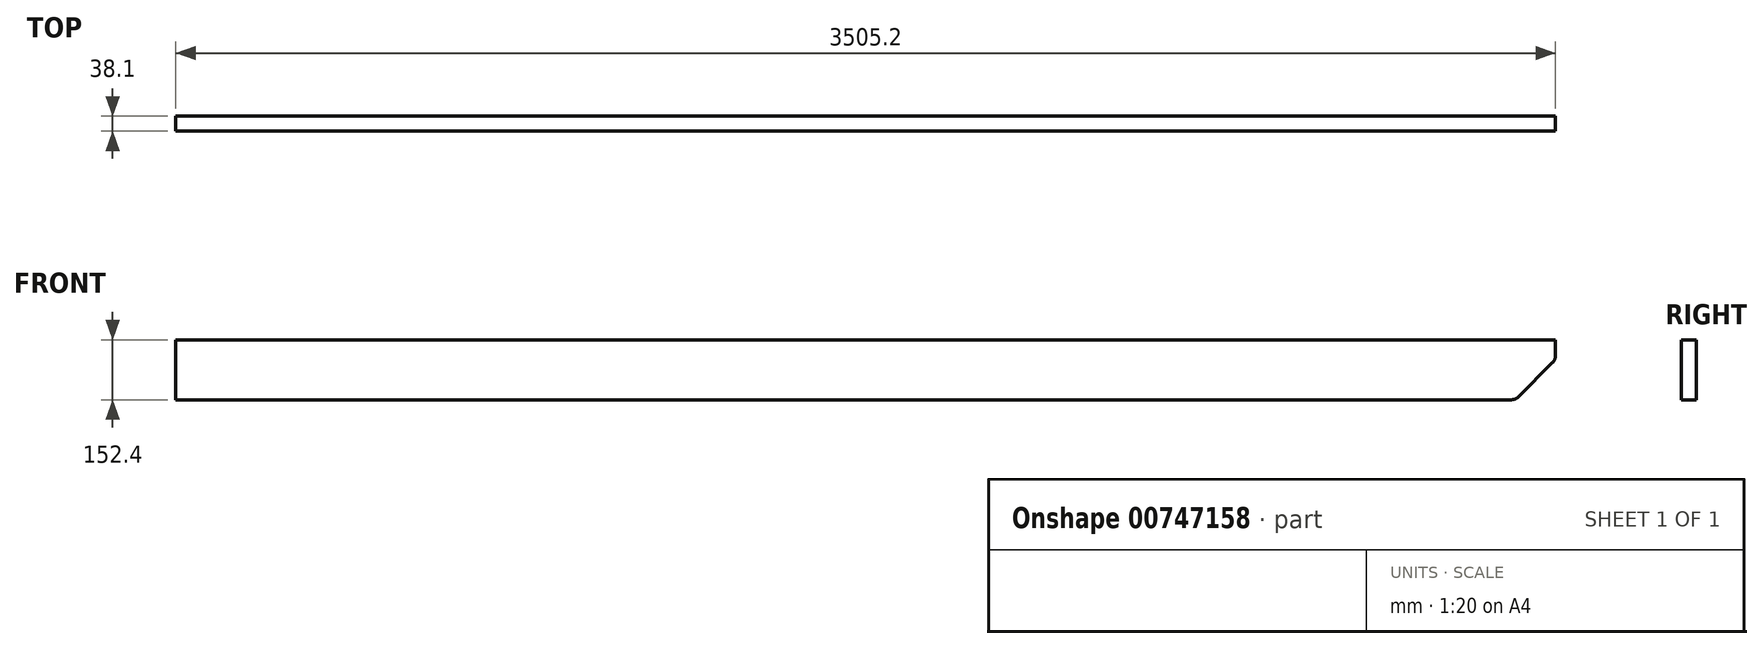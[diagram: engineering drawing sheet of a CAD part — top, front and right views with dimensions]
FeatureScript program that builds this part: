
annotation { "Feature Type Name" : "Feature", "Feature Type Description" : "" }
export const myFeature = defineFeature(function(context is Context, id is Id, definition is map)
    precondition{}
    {
        {
            var Q0;
            Q0=qCreatedBy(makeId("Right.planeOp"),FACE);
            var sketch = newSketch(context, id + "F0", { "sketchPlane" : qUnion([Q0])});
            skLineSegment(sketch, "E0.bottom", {"start": v(-58.55, 100.93) * mm, "end": v(-20.45, 100.93) * mm});
            skLineSegment(sketch, "E0.top", {"start": v(-58.55, -51.47) * mm, "end": v(-20.45, -51.47) * mm});
            skLineSegment(sketch, "E0.left", {"start": v(-58.55, 100.93) * mm, "end": v(-58.55, -51.47) * mm});
            skLineSegment(sketch, "E0.right", {"start": v(-20.45, 100.93) * mm, "end": v(-20.45, -51.47) * mm});
            skSolve(sketch);
        }
        {
            var Q0;
            Q0 = qSketchRegion(id + "F0", true);
            extrude(context, id + "F1", {"entities" : qUnion([Q0]), "oppositeDirection" : true, "depth" : 3505.2 * mm, "offsetDistance" : 25.4 * mm});
        }
        {
            var Q0;
            Q0=makeQuery(id+"F1.opExtrude","CAP_EDGE",EDGE,{"disambiguationData":[OSD([sQuery(id+"F0.wireOp",EDGE,"E0.top")])],"isStart":true});
            chamfer(context, id + "F2", {"entities" : qUnion([Q0]), "width" : 101.6 * mm, "tangentPropagation" : true});
        }
        {
            var Q0;
            {var subQ0=sQuery(id+"F0.wireOp",EDGE,"E0.top");Q0=makeQuery(id+"F2.opChamfer","BLEND_EDGE",EDGE,{"blendedFrom":[makeQuery(id+"F1.opExtrude","CAP_EDGE",EDGE,{"disambiguationData":[OSD([subQ0])],"isStart":true}),makeQuery(id+"F1.opExtrude","CAP_FACE",FACE,{"disambiguationData":[OSD([sQuery(id+"F0.wireOp",EDGE,"E0.bottom"),subQ0,sQuery(id+"F0.wireOp",EDGE,"E0.left"),sQuery(id+"F0.wireOp",EDGE,"E0.right")])],"isStart":true})],"blendedInto":[makeQuery(id+"F1.opExtrude","CAP_FACE",FACE,{"disambiguationData":[OSD([sQuery(id+"F0.wireOp",EDGE,"E0.bottom"),subQ0,sQuery(id+"F0.wireOp",EDGE,"E0.left"),sQuery(id+"F0.wireOp",EDGE,"E0.right")])],"isStart":true})]});}
            var Q1;
            {var subQ0=sQuery(id+"F0.wireOp",EDGE,"E0.top");Q1=makeQuery(id+"F2.opChamfer","BLEND_EDGE",EDGE,{"blendedFrom":[makeQuery(id+"F1.opExtrude","CAP_EDGE",EDGE,{"disambiguationData":[OSD([subQ0])],"isStart":true}),makeQuery(id+"F1.opExtrude","SWEPT_FACE",FACE,{"disambiguationData":[OSD([subQ0])]})],"blendedInto":[makeQuery(id+"F1.opExtrude","SWEPT_FACE",FACE,{"disambiguationData":[OSD([subQ0])]})]});}
            fillet(context, id + "F3", {"entities" : qUnion([Q0, Q1]), "radius" : 25.4 * mm, "tangentPropagation" : true, "allowEdgeOverflow" : false});
        }
    });
